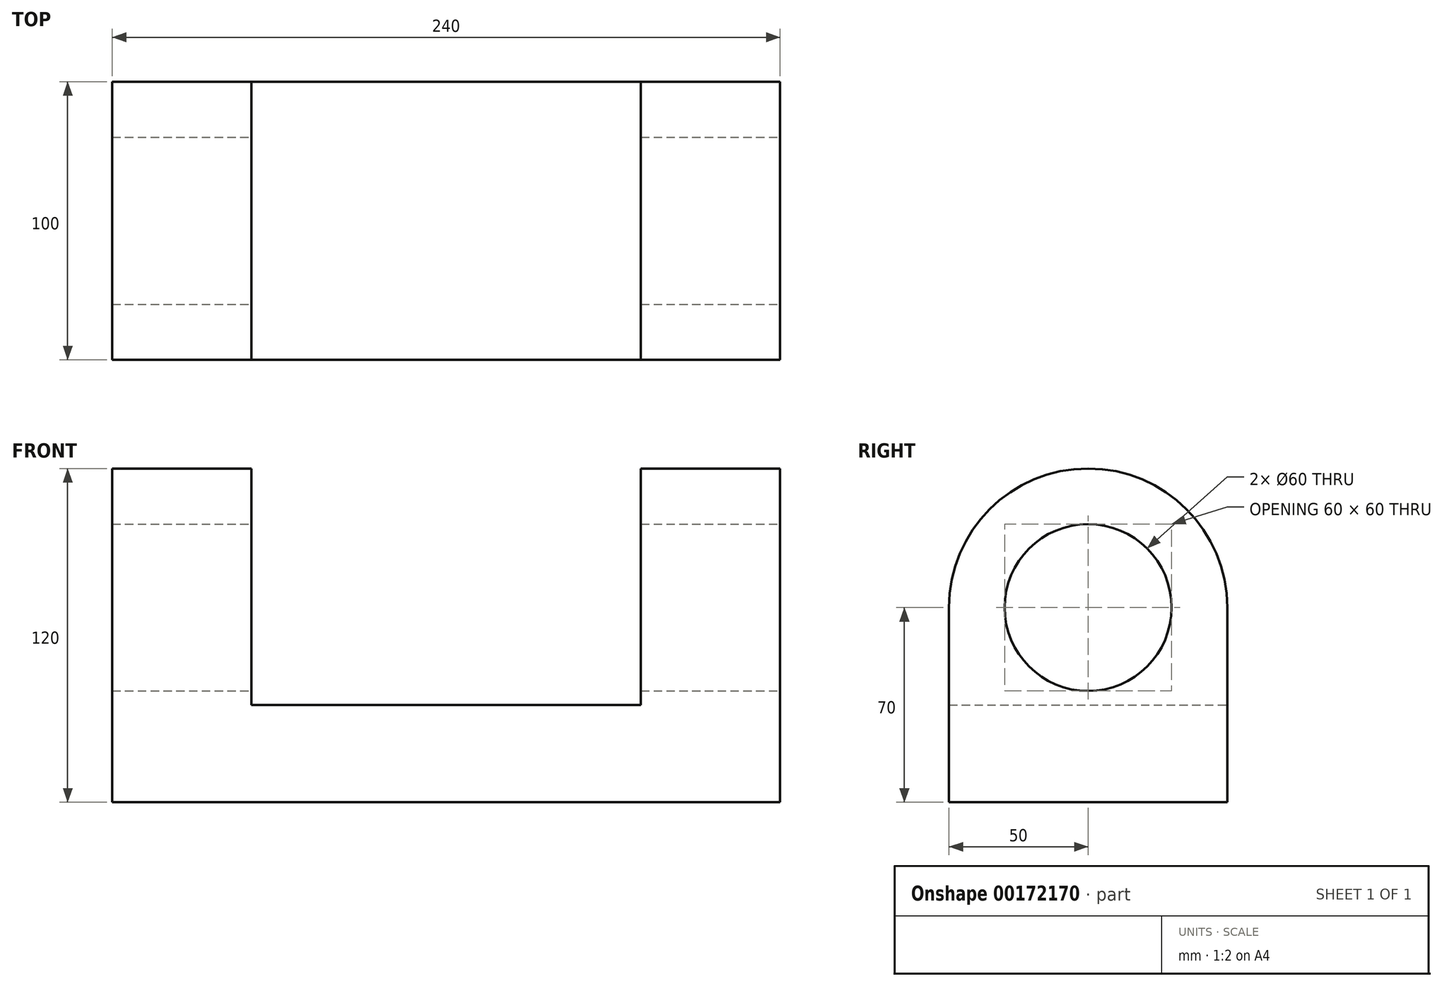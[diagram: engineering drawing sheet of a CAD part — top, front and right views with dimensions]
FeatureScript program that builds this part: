
annotation { "Feature Type Name" : "Feature", "Feature Type Description" : "" }
export const myFeature = defineFeature(function(context is Context, id is Id, definition is map)
    precondition{}
    {
        {
            var Q0;
            Q0=qCreatedBy(makeId("Right.planeOp"),FACE);
            var sketch = newSketch(context, id + "F0", { "sketchPlane" : qUnion([Q0])});
            skLineSegment(sketch, "E0", {"start": v(0, 0) * mm, "end": v(100, 0) * mm});
            skLineSegment(sketch, "E1", {"start": v(0, 0) * mm, "end": v(0, 70) * mm});
            skLineSegment(sketch, "E2", {"start": v(100, 0) * mm, "end": v(100, 70) * mm});
            skArc(sketch, "E3", {"start": v(0, 70) * mm, "mid": v(50, 120) * mm, "end": v(100, 70) * mm});
            skSolve(sketch);
        }
        {
            var Q0;
            Q0 = qSketchRegion(id + "F0", true);
            extrude(context, id + "F1", {"entities" : qUnion([Q0]), "depth" : 240 * mm});
        }
        {
            var Q0;
            Q0=makeQuery(id+"F1.opExtrude","CAP_FACE",FACE,{"disambiguationData":[OSD([sQuery(id+"F0.wireOp",EDGE,"E0"),sQuery(id+"F0.wireOp",EDGE,"E1"),sQuery(id+"F0.wireOp",EDGE,"E2"),sQuery(id+"F0.wireOp",EDGE,"E3")])],"isStart":false});
            var sketch = newSketch(context, id + "F2", { "sketchPlane" : qUnion([Q0])});
            skCircle(sketch, "E4", {"center": v(50, 70) * mm, "radius": 30 * mm});
            skSolve(sketch);
        }
        {
            var Q0;
            Q0 = qSketchRegion(id + "F2", true);
            extrude(context, id + "F3", {"entities" : qUnion([Q0]), "operationType" : NewBodyOperationType.REMOVE, "endBound" : BoundingType.UP_TO_NEXT, "oppositeDirection" : true, "depth" : 25 * mm});
        }
        {
            var Q0;
            Q0=makeQuery(id+"F1.opExtrude","SWEPT_FACE",FACE,{"disambiguationData":[OSD([sQuery(id+"F0.wireOp",EDGE,"E0")])]});
            cPlane(context, id + "F4", {"entities" : qUnion([Q0]), "cplaneType" : CPlaneType.OFFSET, "offset" : 35 * mm, "oppositeDirection" : true, "width" : 150 * mm, "height" : 150 * mm});
        }
        {
            var Q0;
            Q0=qCreatedBy(id+"F4.planeOp",FACE);
            var sketch = newSketch(context, id + "F5", { "sketchPlane" : qUnion([Q0])});
            skLineSegment(sketch, "E5.bottom", {"start": v(50, 0) * mm, "end": v(190, 0) * mm});
            skLineSegment(sketch, "E5.top", {"start": v(50, -100) * mm, "end": v(190, -100) * mm});
            skLineSegment(sketch, "E5.left", {"start": v(50, 0) * mm, "end": v(50, -100) * mm});
            skLineSegment(sketch, "E5.right", {"start": v(190, 0) * mm, "end": v(190, -100) * mm});
            skSolve(sketch);
        }
        {
            var Q0;
            Q0 = qSketchRegion(id + "F5", true);
            extrude(context, id + "F6", {"entities" : qUnion([Q0]), "operationType" : NewBodyOperationType.REMOVE, "endBound" : BoundingType.THROUGH_ALL, "oppositeDirection" : true, "depth" : 25 * mm});
        }
    });
